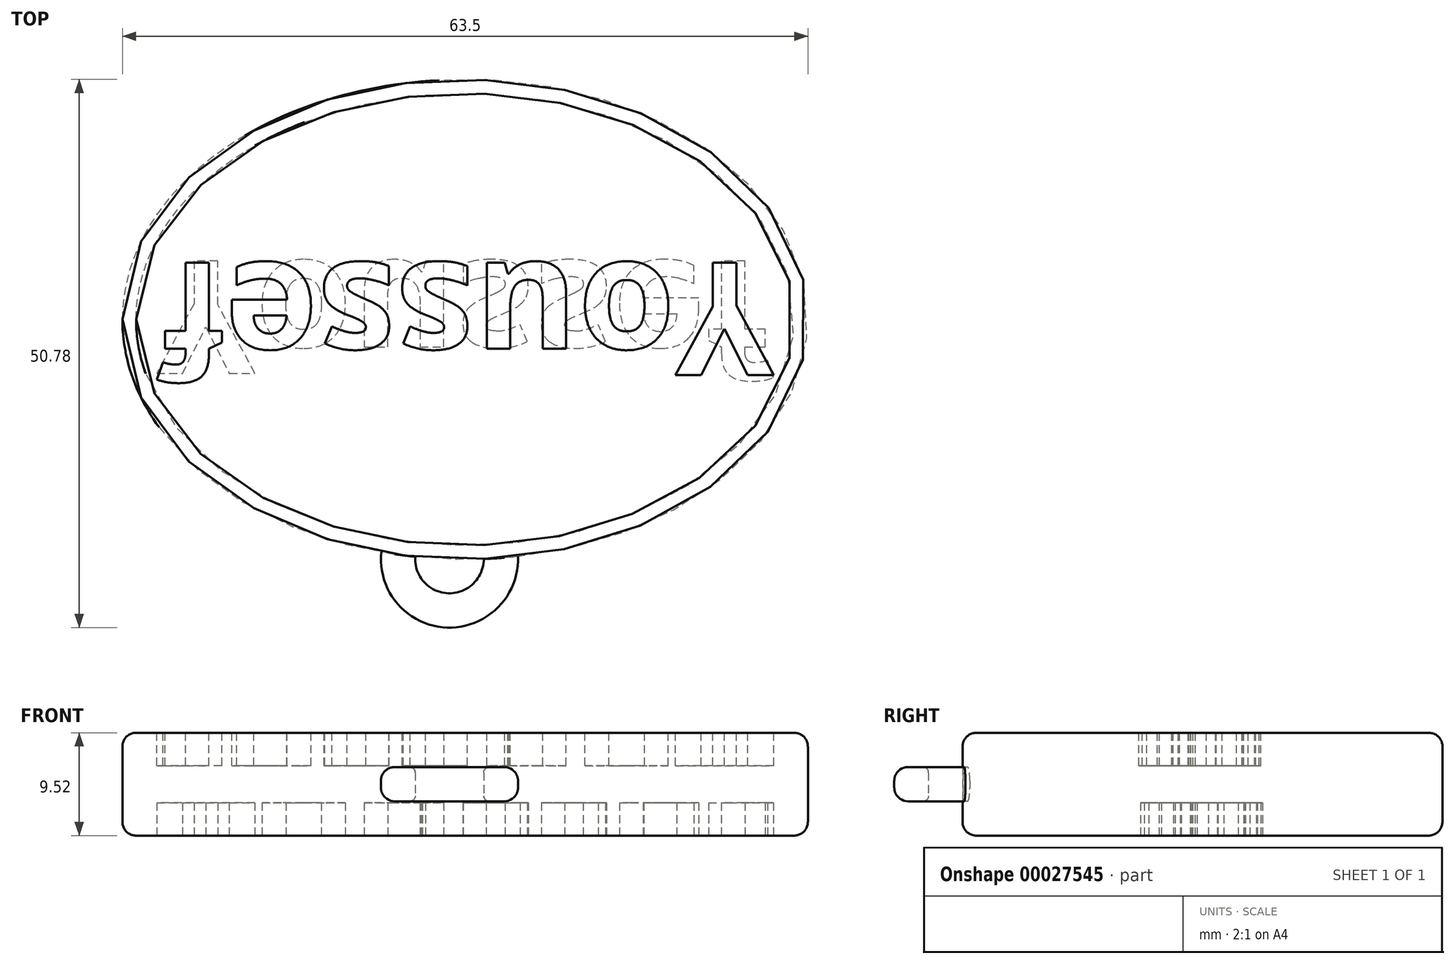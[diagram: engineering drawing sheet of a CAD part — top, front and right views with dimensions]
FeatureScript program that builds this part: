
annotation { "Feature Type Name" : "Feature", "Feature Type Description" : "" }
export const myFeature = defineFeature(function(context is Context, id is Id, definition is map)
    precondition{}
    {
        {
            var Q0;
            Q0=qCreatedBy(makeId("Top.planeOp"),FACE);
            var sketch = newSketch(context, id + "F0", { "sketchPlane" : qUnion([Q0])});
            skEllipse(sketch, "E0", {"center": v(0, 0) * mm, "majorRadius": 31.75 * mm, "minorRadius": 22.23 * mm, "majorAxis": v(-1, 0)});
            skSolve(sketch);
        }
        {
            var Q0;
            Q0=makeQuery(id+"F0.imprint","IMPRINT",FACE,{"disambiguationData":[TD([[makeQuery(id+"F0.imprint","IMPRINT",EDGE,{"derivedFrom":sQuery(id+"F0.wireOp",EDGE,"E0")}),1.0]])]});
            extrude(context, id + "F1", {"entities" : qUnion([Q0]), "endBound" : BoundingType.SYMMETRIC, "depth" : 9.52 * mm});
        }
        {
            var Q0;
            Q0=qCreatedBy(makeId("Top.planeOp"),FACE);
            var sketch = newSketch(context, id + "F2", { "sketchPlane" : qUnion([Q0])});
            skCircle(sketch, "E1", {"center": v(-1.45, -22.2) * mm, "radius": 3.18 * mm});
            skCircle(sketch, "E2", {"center": v(-1.45, -22.2) * mm, "radius": 6.35 * mm});
            skSolve(sketch);
        }
        {
            var Q0;
            Q0=makeQuery(id+"F2.imprint","IMPRINT",FACE,{"disambiguationData":[TD([[makeQuery(id+"F2.imprint","IMPRINT",EDGE,{"derivedFrom":sQuery(id+"F2.wireOp",EDGE,"E1")}),-1.0]])]});
            extrude(context, id + "F3", {"entities" : qUnion([Q0]), "operationType" : NewBodyOperationType.ADD, "endBound" : BoundingType.SYMMETRIC, "depth" : 3.17 * mm});
        }
        {
            var Q0;
            Q0=makeQuery(id+"F1.opExtrude","CAP_FACE",FACE,{"disambiguationData":[OSD([sQuery(id+"F0.wireOp",EDGE,"E0")])],"isStart":true});
            var sketch = newSketch(context, id + "F4", { "sketchPlane" : qUnion([Q0])});
            skText(sketch, "E3", { "text": "Youssef", "fontName": "OpenSans-Bold.ttf"});
            const initialGuessF4  = {"E3": [-0.02857, -0.00542, 1, 0, 0.0105]};
            skSetInitialGuess(sketch, initialGuessF4);
            skSolve(sketch);
        }
        {
            var Q0;
            Q0=makeQuery(id+"F1.opExtrude","CAP_FACE",FACE,{"disambiguationData":[OSD([sQuery(id+"F0.wireOp",EDGE,"E0")])],"isStart":false});
            var sketch = newSketch(context, id + "F5", { "sketchPlane" : qUnion([Q0])});
            skText(sketch, "E4", { "text": "Youssef", "fontName": "OpenSans-Bold.ttf"});
            const initialGuessF5  = {"E4": [0.02858, 0.00525, -1, 0, 0.0105]};
            skSetInitialGuess(sketch, initialGuessF5);
            skSolve(sketch);
        }
        {
            var Q0;
            Q0 = qSketchRegion(id + "F4", true);
            extrude(context, id + "F6", {"entities" : qUnion([Q0]), "operationType" : NewBodyOperationType.REMOVE, "oppositeDirection" : true, "depth" : 3.05 * mm});
        }
        {
            var Q0;
            Q0 = qSketchRegion(id + "F5", true);
            extrude(context, id + "F7", {"entities" : qUnion([Q0]), "operationType" : NewBodyOperationType.REMOVE, "oppositeDirection" : true, "depth" : 3.05 * mm});
        }
        {
            var Q0;
            Q0=makeQuery(id+"F1.opExtrude","CAP_EDGE",EDGE,{"disambiguationData":[OSD([sQuery(id+"F0.wireOp",EDGE,"E0")])],"isStart":true});
            var Q1;
            Q1=makeQuery(id+"F1.opExtrude","CAP_EDGE",EDGE,{"disambiguationData":[OSD([sQuery(id+"F0.wireOp",EDGE,"E0")])],"isStart":false});
            var Q2;
            Q2=makeQuery(id+"F3.opExtrude","CAP_EDGE",EDGE,{"disambiguationData":[OSD([sQuery(id+"F2.wireOp",EDGE,"E2")])],"isStart":true});
            var Q3;
            Q3=makeQuery(id+"F3.opExtrude","CAP_EDGE",EDGE,{"disambiguationData":[OSD([sQuery(id+"F2.wireOp",EDGE,"E2")])],"isStart":false});
            fillet(context, id + "F8", {"entities" : qUnion([Q0, Q1, Q2, Q3]), "radius" : 1.27 * mm, "tangentPropagation" : true, "allowEdgeOverflow" : false});
        }
        {
            var Q0;
            Q0=makeQuery(id+"F3.opExtrude","CAP_EDGE",EDGE,{"disambiguationData":[OSD([sQuery(id+"F2.wireOp",EDGE,"E1")])],"isStart":true});
            var Q1;
            Q1=makeQuery(id+"F3.opExtrude","CAP_EDGE",EDGE,{"disambiguationData":[OSD([sQuery(id+"F2.wireOp",EDGE,"E1")])],"isStart":false});
            fillet(context, id + "F9", {"entities" : qUnion([Q0, Q1]), "radius" : 0.5 * mm, "tangentPropagation" : true, "allowEdgeOverflow" : false});
        }
    });
